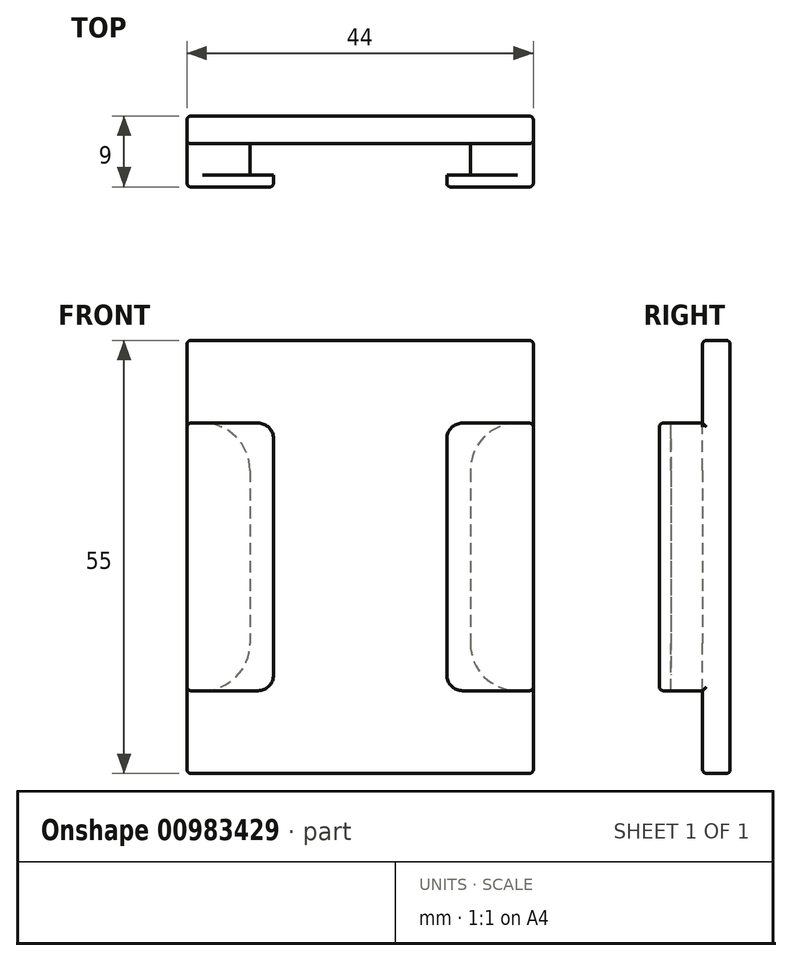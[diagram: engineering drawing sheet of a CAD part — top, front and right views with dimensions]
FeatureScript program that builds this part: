
annotation { "Feature Type Name" : "Feature", "Feature Type Description" : "" }
export const myFeature = defineFeature(function(context is Context, id is Id, definition is map)
    precondition{}
    {
        {
            var Q0;
            Q0=qCreatedBy(makeId("Front.planeOp"),FACE);
            var sketch = newSketch(context, id + "F0", { "sketchPlane" : qUnion([Q0])});
            skLineSegment(sketch, "E0.bottom", {"start": v(0, 0) * mm, "end": v(22, 0) * mm});
            skLineSegment(sketch, "E0.top", {"start": v(0, -55) * mm, "end": v(22, -55) * mm});
            skLineSegment(sketch, "E0.left", {"start": v(0, 0) * mm, "end": v(0, -55) * mm});
            skLineSegment(sketch, "E0.right", {"start": v(22, 0) * mm, "end": v(22, -55) * mm});
            skSolve(sketch);
        }
        {
            var Q0;
            Q0 = qSketchRegion(id + "F0", true);
            extrude(context, id + "F1", {"entities" : qUnion([Q0]), "depth" : 3.5 * mm, "offsetDistance" : 25 * mm});
        }
        {
            var Q0;
            Q0=makeQuery(id+"F1.opExtrude","CAP_FACE",FACE,{"disambiguationData":[OSD([sQuery(id+"F0.wireOp",EDGE,"E0.bottom"),sQuery(id+"F0.wireOp",EDGE,"E0.top"),sQuery(id+"F0.wireOp",EDGE,"E0.left"),sQuery(id+"F0.wireOp",EDGE,"E0.right")])],"isStart":false});
            var sketch = newSketch(context, id + "F2", { "sketchPlane" : qUnion([Q0])});
            skLineSegment(sketch, "E1.bottom", {"start": v(0, -10.5) * mm, "end": v(2, -10.5) * mm});
            skLineSegment(sketch, "E1.top", {"start": v(0, -44.5) * mm, "end": v(2, -44.5) * mm});
            skLineSegment(sketch, "E1.left", {"start": v(0, -10.5) * mm, "end": v(0, -44.5) * mm});
            skLineSegment(sketch, "E1.right", {"start": v(8, -16.5) * mm, "end": v(8, -38.5) * mm});
            skPoint(sketch, "E2.visualSharp", {"position": v(8, -10.5) * mm});
            skArc(sketch, "E2.filletArc", {"start": v(8, -16.5) * mm, "mid": v(6.24, -12.26) * mm, "end": v(2, -10.5) * mm});
            skPoint(sketch, "E3.visualSharp", {"position": v(8, -44.5) * mm});
            skArc(sketch, "E3.filletArc", {"start": v(2, -44.5) * mm, "mid": v(6.24, -42.74) * mm, "end": v(8, -38.5) * mm});
            skSolve(sketch);
        }
        {
            var Q0;
            Q0 = qSketchRegion(id + "F2", true);
            extrude(context, id + "F3", {"entities" : qUnion([Q0]), "operationType" : NewBodyOperationType.ADD, "depth" : 4 * mm, "offsetDistance" : 25 * mm});
        }
        {
            var Q0;
            Q0=makeQuery(id+"F3.opExtrude","CAP_FACE",FACE,{"disambiguationData":[OSD([sQuery(id+"F2.wireOp",EDGE,"E1.bottom"),sQuery(id+"F2.wireOp",EDGE,"E1.top"),sQuery(id+"F2.wireOp",EDGE,"E1.left"),sQuery(id+"F2.wireOp",EDGE,"E1.right")])],"isStart":false});
            var sketch = newSketch(context, id + "F4", { "sketchPlane" : qUnion([Q0])});
            skLineSegment(sketch, "E4.bottom", {"start": v(0, -10.5) * mm, "end": v(9, -10.5) * mm});
            skLineSegment(sketch, "E4.top", {"start": v(0, -44.5) * mm, "end": v(9, -44.5) * mm});
            skLineSegment(sketch, "E4.left", {"start": v(0, -10.5) * mm, "end": v(0, -44.5) * mm});
            skLineSegment(sketch, "E4.right", {"start": v(11, -12.5) * mm, "end": v(11, -42.5) * mm});
            skPoint(sketch, "E5.visualSharp", {"position": v(11, -10.5) * mm});
            skArc(sketch, "E5.filletArc", {"start": v(11, -12.5) * mm, "mid": v(10.41, -11.09) * mm, "end": v(9, -10.5) * mm});
            skPoint(sketch, "E6.visualSharp", {"position": v(11, -44.5) * mm});
            skArc(sketch, "E6.filletArc", {"start": v(9, -44.5) * mm, "mid": v(10.41, -43.91) * mm, "end": v(11, -42.5) * mm});
            skSolve(sketch);
        }
        {
            var Q0;
            Q0 = qSketchRegion(id + "F4", true);
            extrude(context, id + "F5", {"entities" : qUnion([Q0]), "operationType" : NewBodyOperationType.ADD, "depth" : 1.5 * mm, "offsetDistance" : 25 * mm});
        }
        {
            var Q0;
            Q0=makeQuery(id+"F5.opExtrude","CAP_FACE",FACE,{"disambiguationData":[OSD([sQuery(id+"F4.wireOp",EDGE,"E4.bottom"),sQuery(id+"F4.wireOp",EDGE,"E4.top"),sQuery(id+"F4.wireOp",EDGE,"E4.left"),sQuery(id+"F4.wireOp",EDGE,"E4.right"),sQuery(id+"F4.wireOp",EDGE,"E5.filletArc"),sQuery(id+"F4.wireOp",EDGE,"E6.filletArc")])],"isStart":false});
            var Q1;
            Q1=makeQuery(id+"F5.boolean.opBoolean","MERGE",FACE,{"derivedFrom":[makeQuery(id+"F3.boolean.opBoolean","MERGE",FACE,{"derivedFrom":[makeQuery(id+"F1.opExtrude","SWEPT_FACE",FACE,{"disambiguationData":[OSD([sQuery(id+"F0.wireOp",EDGE,"E0.left")])]}),makeQuery(id+"F3.opExtrude","SWEPT_FACE",FACE,{"disambiguationData":[OSD([sQuery(id+"F2.wireOp",EDGE,"E1.left")])]})]}),makeQuery(id+"F5.opExtrude","SWEPT_FACE",FACE,{"disambiguationData":[OSD([sQuery(id+"F4.wireOp",EDGE,"E4.left")])]})]});
            fillet(context, id + "F6", {"entities" : qUnion([Q0, Q1]), "radius" : 0.5 * mm, "tangentPropagation" : true, "allowEdgeOverflow" : false});
        }
        {
            var Q0;
            Q0=makeQuery(id+"F1.opExtrude","SWEPT_BODY",BODY,{"disambiguationData":[OSD([sQuery(id+"F0.wireOp",EDGE,"E0.bottom"),sQuery(id+"F0.wireOp",EDGE,"E0.top"),sQuery(id+"F0.wireOp",EDGE,"E0.left"),sQuery(id+"F0.wireOp",EDGE,"E0.right")])]});
            var Q1;
            Q1=makeQuery(id+"F1.opExtrude","SWEPT_FACE",FACE,{"disambiguationData":[OSD([sQuery(id+"F0.wireOp",EDGE,"E0.right")])]});
            mirror(context, id + "F7", {"operationType" : NewBodyOperationType.ADD, "entities" : qUnion([Q0]), "mirrorPlane" : qUnion([Q1])});
        }
        {
            var Q0;
            {var subQ0=makeQuery(id+"F1.opExtrude","SWEPT_FACE",FACE,{"disambiguationData":[OSD([sQuery(id+"F0.wireOp",EDGE,"E0.top")])]});Q0=makeQuery(id+"F7.boolean.opBoolean","MERGE",FACE,{"derivedFrom":[subQ0,makeQuery(id+"F7.opPattern","COPY",FACE,{"derivedFrom":subQ0,"instanceName":"1"})]});}
            var Q1;
            {var subQ0=makeQuery(id+"F1.opExtrude","SWEPT_FACE",FACE,{"disambiguationData":[OSD([sQuery(id+"F0.wireOp",EDGE,"E0.bottom")])]});Q1=makeQuery(id+"F7.boolean.opBoolean","MERGE",FACE,{"derivedFrom":[subQ0,makeQuery(id+"F7.opPattern","COPY",FACE,{"derivedFrom":subQ0,"instanceName":"1"})]});}
            fillet(context, id + "F8", {"entities" : qUnion([Q0, Q1]), "radius" : 0.5 * mm, "tangentPropagation" : true, "allowEdgeOverflow" : false});
        }
    });
